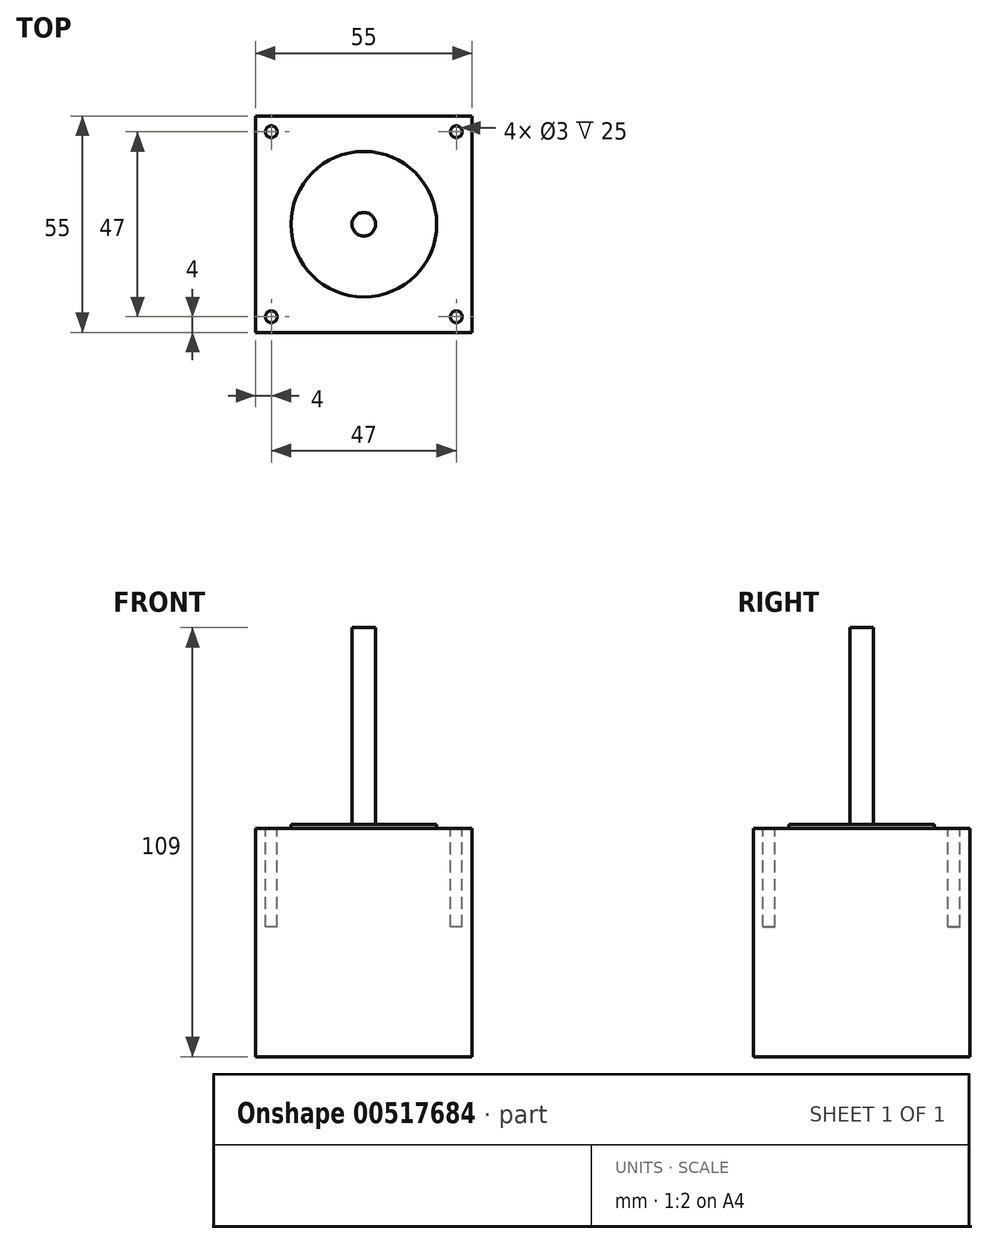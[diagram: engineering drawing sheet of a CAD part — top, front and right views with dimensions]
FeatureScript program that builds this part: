
annotation { "Feature Type Name" : "Feature", "Feature Type Description" : "" }
export const myFeature = defineFeature(function(context is Context, id is Id, definition is map)
    precondition{}
    {
        {
            var Q0;
            Q0=qCreatedBy(makeId("Top.planeOp"),FACE);
            var sketch = newSketch(context, id + "F0", { "sketchPlane" : qUnion([Q0])});
            skLineSegment(sketch, "E0.bottom", {"start": v(0, 0) * mm, "end": v(55, 0) * mm});
            skLineSegment(sketch, "E0.top", {"start": v(0, 55) * mm, "end": v(55, 55) * mm});
            skLineSegment(sketch, "E0.left", {"start": v(0, 0) * mm, "end": v(0, 55) * mm});
            skLineSegment(sketch, "E0.right", {"start": v(55, 0) * mm, "end": v(55, 55) * mm});
            skSolve(sketch);
        }
        {
            var Q0;
            Q0=makeQuery(id+"F0.imprint","IMPRINT",FACE,{"disambiguationData":[TD([[makeQuery(id+"F0.imprint","IMPRINT",EDGE,{"derivedFrom":sQuery(id+"F0.wireOp",EDGE,"E0.bottom")}),1.0]])]});
            extrude(context, id + "F1", {"entities" : qUnion([Q0]), "depth" : 58 * mm, "offsetDistance" : 25 * mm});
        }
        {
            var Q0;
            Q0=makeQuery(id+"F1.opExtrude","CAP_FACE",FACE,{"disambiguationData":[OSD([sQuery(id+"F0.wireOp",EDGE,"E0.bottom"),sQuery(id+"F0.wireOp",EDGE,"E0.top"),sQuery(id+"F0.wireOp",EDGE,"E0.left"),sQuery(id+"F0.wireOp",EDGE,"E0.right")])],"isStart":false});
            var sketch = newSketch(context, id + "F2", { "sketchPlane" : qUnion([Q0])});
            skCircle(sketch, "E1", {"center": v(27.5, 27.5) * mm, "radius": 18.5 * mm});
            skLineSegment(sketch, "E2", {"start": v(27.5, 55) * mm, "end": v(27.5, 27.5) * mm, "construction": true});
            skLineSegment(sketch, "E3", {"start": v(27.5, 27.5) * mm, "end": v(0, 27.5) * mm, "construction": true});
            skSolve(sketch);
        }
        {
            var Q0;
            Q0 = qSketchRegion(id + "F2", true);
            extrude(context, id + "F3", {"entities" : qUnion([Q0]), "operationType" : NewBodyOperationType.ADD, "depth" : 1 * mm, "offsetDistance" : 25 * mm});
        }
        {
            var Q0;
            Q0=makeQuery(id+"F3.opExtrude","CAP_FACE",FACE,{"disambiguationData":[OSD([sQuery(id+"F2.wireOp",EDGE,"E1")])],"isStart":false});
            var sketch = newSketch(context, id + "F4", { "sketchPlane" : qUnion([Q0])});
            skCircle(sketch, "E4", {"center": v(27.5, 27.5) * mm, "radius": 3 * mm});
            skSolve(sketch);
        }
        {
            var Q0;
            Q0 = qSketchRegion(id + "F4", true);
            extrude(context, id + "F5", {"entities" : qUnion([Q0]), "operationType" : NewBodyOperationType.ADD, "depth" : 50 * mm, "offsetDistance" : 25 * mm});
        }
        {
            var Q0;
            Q0=makeQuery(id+"F1.opExtrude","CAP_FACE",FACE,{"disambiguationData":[OSD([sQuery(id+"F0.wireOp",EDGE,"E0.bottom"),sQuery(id+"F0.wireOp",EDGE,"E0.top"),sQuery(id+"F0.wireOp",EDGE,"E0.left"),sQuery(id+"F0.wireOp",EDGE,"E0.right")])],"isStart":false});
            var sketch = newSketch(context, id + "F6", { "sketchPlane" : qUnion([Q0])});
            skCircle(sketch, "E5", {"center": v(4, 51) * mm, "radius": 1.5 * mm});
            skCircle(sketch, "E6.1.0", {"center": v(4, 4) * mm, "radius": 1.5 * mm});
            skCircle(sketch, "E6.2.0", {"center": v(51, 4) * mm, "radius": 1.5 * mm});
            skCircle(sketch, "E6.3.0", {"center": v(51, 51) * mm, "radius": 1.5 * mm});
            skPoint(sketch, "E6.center", {"position": v(27.5, 27.5) * mm});
            skSolve(sketch);
        }
        {
            var Q0;
            Q0 = qSketchRegion(id + "F6", true);
            extrude(context, id + "F7", {"entities" : qUnion([Q0]), "operationType" : NewBodyOperationType.REMOVE, "oppositeDirection" : true, "depth" : 25 * mm, "offsetDistance" : 25 * mm});
        }
    });
